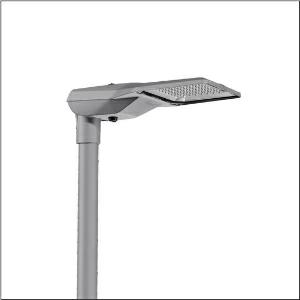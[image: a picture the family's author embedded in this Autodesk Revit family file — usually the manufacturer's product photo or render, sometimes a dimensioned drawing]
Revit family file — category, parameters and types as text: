
# Revit family: streetlight_sl_21_iq_midi___st1_5a_5xe3p31y08mb_5967
name_source: partatom
category: Lighting Fixtures
units: mm (PartAtom-declared; Revit-internal decimal feet)

## family parameters
Cut with Voids When Loaded = No
Host = Face
Light Source = No
Part Type = Normal
Room Calculation Point = No
Round Connector Dimension = Use Diameter
Shared = No

## types (1)
- --- (1 x LED, 18020 lm, 129.3 W, 3000K)
    Apparent Load = 129 VA
    CIE Flux Codes = 22 53 95 100 100
    Color Rendering = 70
    Color Temperature = 3000K
    Default Elevation = 1800 mm
    Description = Streetlight SL 21 iQ midi, mast luminaire, primary light control with lens, of PMMA, primary optical cover: cover, of toughened safety glass, transparent, light distribution: ST1.5a, light emission: direct distribution, primary light characteristic: asymmetric, installation type: post-top, side-entry, LED, High Power LED, rated luminous flux: 18.020lm, luminous efficacy: 139lm/W, light colour: 730, colour temperature: 3000K, control: presetting dimming logarithmic, Street-Remote, Auto-Match, Temp-Guard, Lumen-Switch, Night-Set, Smart-Wire, Light-Fading, Desk-Remote (wireless, voltage-free reading and setting of iQ features in the workshop via application-optimized NFC function/RFID function), optimised constant luminous flux control (CLO 2.0), mains connection: 230..240V, AC, 50/60Hz, start of lifetime: 129W, end of service life: 142W, reduction: 56W, luminaire housing, of diecast aluminium, powder-coated, Siteco® metallic grey (DB 702S), corrosivity category C5 mid according to DIN EN ISO 12944, please order mast flange separately, inclination adjustable: 0°, 5°, 10°, 15°, sealing non-destructively replaceable, multi-level sealing system, length: 644mm, width: 335mm, height: 110mm, mast flange for spigot size: 42mm (side-entry): 5XC10008XM4, 60/48mm (side-entry/post-top): 5XC10108XM2, 76/60mm (side-entry/post-top): 5XC10108XM1, Smart Interface below and above, protection rating (complete): IP66, insulation class (complete): insulation class II (safety insulation), certification: CE, ENEC, ENEC+, VDE, impact resistance: IK09, permissible operating ambient temperature for outdoor applications: -40..+50°C, standard-compliant lighting for roads and squares, packaging unit: 1 piece

Light Distribution: ST1.5a
    Height = 111 mm
    Lamp = 1 x LED
    Lamp Light Flux = 18020 lm
    Lamp Power = 129.3 W
    Lamp count = 1
    Length = 644 mm
    Luminous efficacy = 139 lm/W
    Manufacturer = Siteco
    ModVariant = No
    Model = 5XE3P31Y08MB
    Number of Poles = 1
    OnlyDefault = Yes
    Power Factor = 1
    Product Name = Streetlight SL 21 iQ midi | ST1.5a
    Product group = mast luminaire | pylon top
    ProductGroupID = 6100
    Protection Class = Protection class II
    Protection Degree = IP 66
    RLX_Detail_Level = 1
    RLX_Emergency_Light_Flux = 0 lm
    RLX_Emergency_Type = 0
    RLX_Emergency_Type_DB = No
    RlxData = <blob elided: 94497 chars, md5=945a2bc4>
    Socket = socket
    Standby Power = 0 W
    System Light Flux = 18021 lm
    System Power = 129 W
    Type Comments = factory setting: luminous flux: 100 % | dim-lin: 254 | 672 mA
    Type Image = l_1004304.jpg
    URL = http://relux.com
    VarID = @adj_041949
    Voltage = 0 V
    Weight = 0.00 kg
    Width = 336 mm

## geometry (parser evidence)
native form markers: Blend x4, Sweep x13
no freeform markers — native parametric forms only
